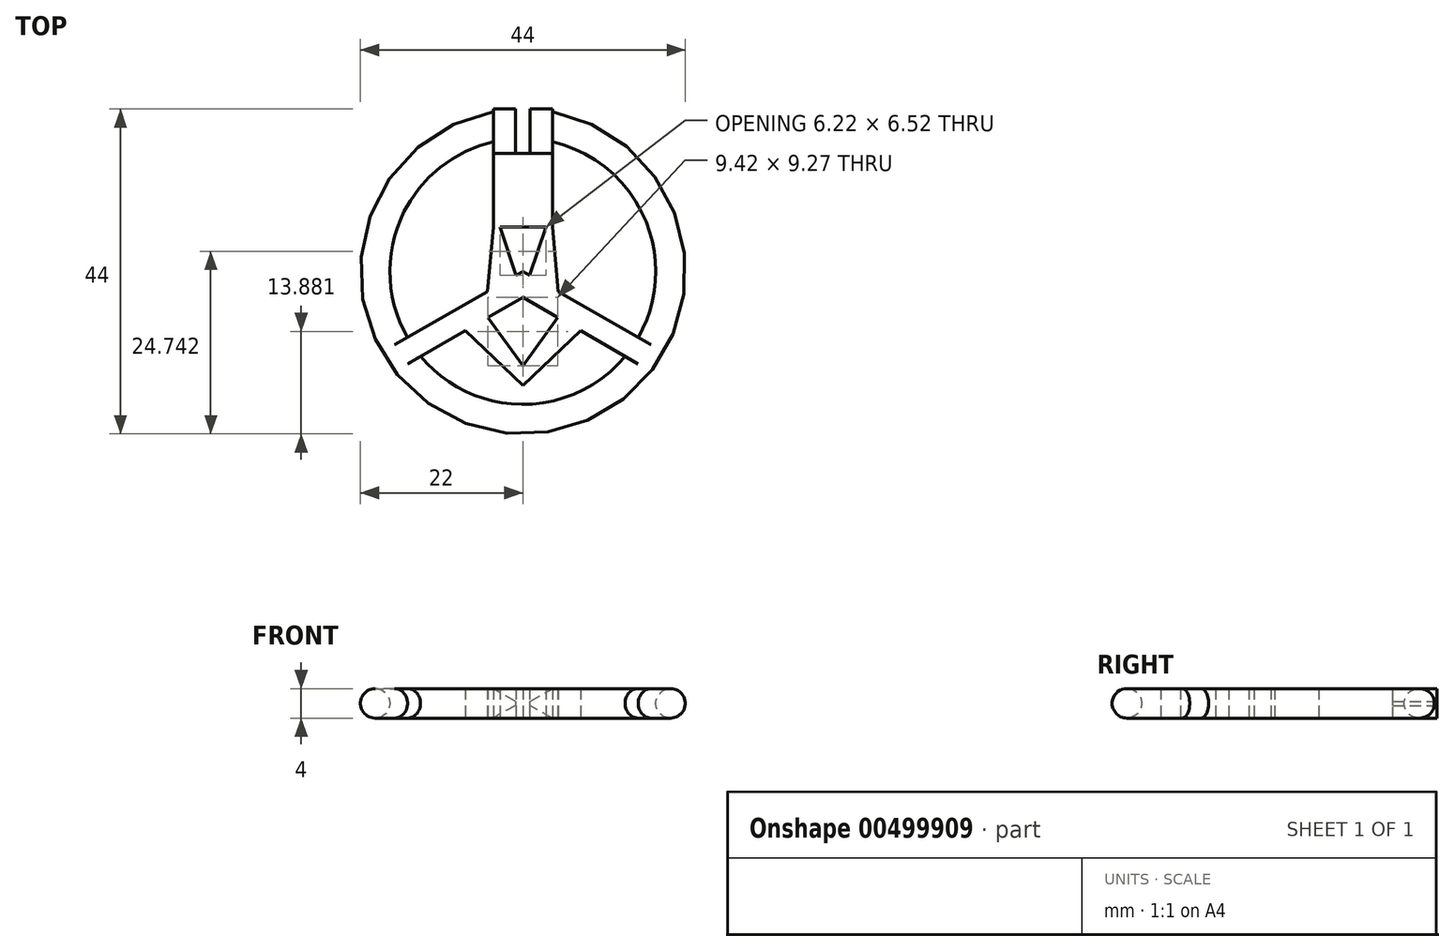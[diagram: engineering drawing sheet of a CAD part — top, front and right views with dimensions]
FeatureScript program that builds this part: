
annotation { "Feature Type Name" : "Feature", "Feature Type Description" : "" }
export const myFeature = defineFeature(function(context is Context, id is Id, definition is map)
    precondition{}
    {
        {
            var Q0;
            Q0=qCreatedBy(makeId("Top.planeOp"),FACE);
            var sketch = newSketch(context, id + "F0", { "sketchPlane" : qUnion([Q0])});
            skCircle(sketch, "E0", {"center": v(0, 0) * mm, "radius": 20 * mm});
            skLineSegment(sketch, "E1", {"start": v(0, 6) * mm, "end": v(3.11, 6) * mm});
            skLineSegment(sketch, "E2", {"start": v(0, 6) * mm, "end": v(-3.11, 6) * mm});
            skLineSegment(sketch, "E3", {"start": v(-4, 6) * mm, "end": v(-4, 22) * mm});
            skLineSegment(sketch, "E4", {"start": v(4, 6) * mm, "end": v(4, 22) * mm});
            skLineSegment(sketch, "E5", {"start": v(4, 22) * mm, "end": v(-4, 22) * mm});
            skLineSegment(sketch, "E6", {"start": v(17.36, -9.94) * mm, "end": v(4.8, -2.75) * mm});
            skLineSegment(sketch, "E7", {"start": v(0, 0) * mm, "end": v(0, -19.04) * mm});
            skLineSegment(sketch, "E8.MirrorCS", {"start": v(-17.36, -9.94) * mm, "end": v(-4.8, -2.75) * mm});
            skLineSegment(sketch, "E9", {"start": v(-15.6, -12.51) * mm, "end": v(-7.8, -8) * mm});
            skLineSegment(sketch, "E10.MirrorCS", {"start": v(15.6, -12.51) * mm, "end": v(7.8, -8) * mm});
            skLineSegment(sketch, "E11", {"start": v(4.7, -6.2) * mm, "end": v(0, -12.75) * mm});
            skLineSegment(sketch, "E12", {"start": v(7.8, -8) * mm, "end": v(0, -15.44) * mm});
            skLineSegment(sketch, "E13.MirrorCS", {"start": v(-4.7, -6.2) * mm, "end": v(0, -12.75) * mm});
            skLineSegment(sketch, "E14.MirrorCS", {"start": v(-7.8, -8) * mm, "end": v(0, -15.44) * mm});
            skLineSegment(sketch, "E15.trimOffspring", {"start": v(4.7, -6.2) * mm, "end": v(0, -3.48) * mm});
            skLineSegment(sketch, "E16.trimOffspring", {"start": v(-4.7, -6.2) * mm, "end": v(0, -3.48) * mm});
            skLineSegment(sketch, "E17", {"start": v(4, 6) * mm, "end": v(4.8, -2.75) * mm});
            skLineSegment(sketch, "E18.MirrorCS", {"start": v(-4, 6) * mm, "end": v(-4.8, -2.75) * mm});
            skLineSegment(sketch, "E19", {"start": v(3.11, 6) * mm, "end": v(0.9, -0.52) * mm});
            skLineSegment(sketch, "E20.MirrorCS", {"start": v(-3.11, 6) * mm, "end": v(-0.9, -0.52) * mm});
            skLineSegment(sketch, "E21.trimOffspring", {"start": v(-0.9, -0.52) * mm, "end": v(0, 0) * mm});
            skLineSegment(sketch, "E22.trimOffspring", {"start": v(0.9, -0.52) * mm, "end": v(0, 0) * mm});
            skSolve(sketch);
        }
        {
            var Q0;
            Q0=qCreatedBy(makeId("Front.planeOp"),FACE);
            var sketch = newSketch(context, id + "F1", { "sketchPlane" : qUnion([Q0])});
            skLineSegment(sketch, "E23", {"start": v(0, 0) * mm, "end": v(-20, 0) * mm});
            skCircle(sketch, "E24", {"center": v(-20, 0) * mm, "radius": 2 * mm});
            skSolve(sketch);
        }
        {
            var Q0;
            Q0=makeQuery(id+"F1.imprint","IMPRINT",FACE,{"disambiguationData":[TD([[makeQuery(id+"F1.imprint","IMPRINT",EDGE,{"derivedFrom":sQuery(id+"F1.wireOp",EDGE,"E24")}),1.0]])]});
            var Q1;
            Q1=sQuery(id+"F0.wireOp",EDGE,"E0");
            revolve(context, id + "F2", {"entities" : qUnion([Q0]), "axis" : qUnion([Q1]), "revolveType" : RevolveType.FULL});
        }
        {
            var Q0;
            {var subQ5=sQuery(id+"F0.wireOp",EDGE,"E5");Q0=makeQuery(id+"F0.imprint","IMPRINT",FACE,{"disambiguationData":[TD([[makeQuery(id+"F0.imprint","IMPRINT",EDGE,{"derivedFrom":subQ5}),1.0]])]});}
            var Q1;
            {var subQ4=sQuery(id+"F0.wireOp",EDGE,"E1");Q1=makeQuery(id+"F0.imprint","IMPRINT",FACE,{"disambiguationData":[TD([[makeQuery(id+"F0.imprint","IMPRINT",EDGE,{"derivedFrom":subQ4}),1.0]])]});}
            extrude(context, id + "F3", {"entities" : qUnion([Q0, Q1]), "operationType" : NewBodyOperationType.ADD, "depth" : 2 * mm, "hasSecondDirection" : true, "secondDirectionOppositeDirection" : true, "secondDirectionDepth" : 2 * mm});
        }
        {
            var Q0;
            Q0=makeQuery(id+"F3.opExtrude","SWEPT_FACE",FACE,{"disambiguationData":[OSD([sQuery(id+"F0.wireOp",EDGE,"E5")])]});
            var sketch = newSketch(context, id + "F4", { "sketchPlane" : qUnion([Q0])});
            skLineSegment(sketch, "E25", {"start": v(-4, -2) * mm, "end": v(4, -2) * mm});
            skLineSegment(sketch, "E26", {"start": v(4, 2) * mm, "end": v(-4, 2) * mm});
            skLineSegment(sketch, "E27", {"start": v(1, 0.29) * mm, "end": v(4, 2) * mm});
            skLineSegment(sketch, "E28", {"start": v(1, -0.29) * mm, "end": v(4, -2) * mm});
            skLineSegment(sketch, "E29", {"start": v(4, -2) * mm, "end": v(-4, -2) * mm});
            skLineSegment(sketch, "E30", {"start": v(-4, -2) * mm, "end": v(-1, -0.29) * mm});
            skLineSegment(sketch, "E31", {"start": v(-1, 0.29) * mm, "end": v(-4, 2) * mm});
            skLineSegment(sketch, "E32", {"start": v(-4, 2) * mm, "end": v(4, 2) * mm});
            skLineSegment(sketch, "E33", {"start": v(0, 2) * mm, "end": v(0, -2) * mm});
            skLineSegment(sketch, "E34", {"start": v(-1, 0) * mm, "end": v(-1, 0.29) * mm});
            skLineSegment(sketch, "E35", {"start": v(-1, 0) * mm, "end": v(-1, -0.29) * mm});
            skLineSegment(sketch, "E36.MirrorCS", {"start": v(1, 0) * mm, "end": v(1, 0.29) * mm});
            skLineSegment(sketch, "E37.MirrorCS", {"start": v(1, 0) * mm, "end": v(1, -0.29) * mm});
            skSolve(sketch);
        }
        {
            var Q0;
            Q0=makeQuery(id+"F4.imprint","IMPRINT",FACE,{"disambiguationData":[TD([[makeQuery(id+"F4.imprint","IMPRINT",EDGE,{"derivedFrom":sQuery(id+"F4.wireOp",EDGE,"E27")}),1.0]])]});
            var Q1;
            {var subQ5=sQuery(id+"F4.wireOp",EDGE,"E30");Q1=makeQuery(id+"F4.imprint","IMPRINT",FACE,{"disambiguationData":[TD([[makeQuery(id+"F4.imprint","IMPRINT",EDGE,{"derivedFrom":subQ5}),-1.0]])]});}
            extrude(context, id + "F5", {"entities" : qUnion([Q0, Q1]), "operationType" : NewBodyOperationType.REMOVE, "oppositeDirection" : true, "depth" : 6 * mm});
        }
    });
